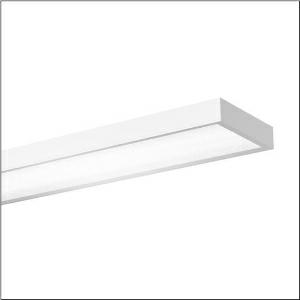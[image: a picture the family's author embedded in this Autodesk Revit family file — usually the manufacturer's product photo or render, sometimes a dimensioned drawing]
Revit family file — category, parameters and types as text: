
# Revit family: sport_31_51hs12dd4gca
name_source: partatom
category: Lighting Fixtures
units: mm (PartAtom-declared; Revit-internal decimal feet)

## family parameters
Cut with Voids When Loaded = No
Host = Face
Light Source = No
Part Type = Normal
Room Calculation Point = No
Round Connector Dimension = Use Diameter
Shared = No

## types (1)
- --- (1 x LED, 15290 lm, 113 W, 4000K)
    Apparent Load = 113 VA
    CIE Flux Codes = 65 89 97 100 100
    Color Rendering = 80
    Color Temperature = 4000K
    Default Elevation = 1800 mm
    Description = Sport 31, high bay luminaire, primary light control with reflector, of sheet steel, primary anti-glare with prismatic structure, of PC, primary optical cover: cover panel, of PC, light emission: direct distribution, primary light characteristic: symmetric, installation type: suspended mounting, recessed, surface-mounted, LED, rated luminous flux: 16.000lm, luminous efficacy: 137lm/W, light colour: 840, colour temperature: 4000K, control gear: DALI 2, with terminal, 5-pole, max. 2.5mm², mains connection: 220..240V, AC/DC, 50/60Hz, rated input power: 117W, housing, of sheet steel, traffic white (RAL 9016), length: 1.540mm, width: 415mm, height: 95mm, protection rating (complete): IP20, protection rating (lamp compartment, on room side): IP50, insulation class (complete): insulation class I (protective earthing), certification: CE, ENEC, UKCA, ball protection: ball impact resistant with ceiling mounting or chain suspension, impact resistance: IK08, permissible operating ambient temperature: -20..+35°C, standard: DIN 18032-3, EN 60598-2-22, packaging unit: 1 piece
    Height = 100 mm  [stored 0.328084 ft]
    Lamp = 1 x LED
    Lamp Light Flux = 15290 lm
    Lamp Power = 113 W
    Lamp count = 1
    Length = 1500 mm
    Luminous efficacy = 135 lm/W
    Manufacturer = Siteco
    ModVariant = No
    Model = 51HS12DD4GCA
    Mounting Place = Ceiling
    Mounting Type = Pendant
    Number of Poles = 1
    OnlyDefault = Yes
    Power Factor = 1
    Product Name = Sport 31
    Product group = high bay luminaire
    ProductGroupID = 901
    Protection Class = Protection class I
    Protection Degree = IP 20
    RLX_Detail_Level = 1
    RLX_Emergency_Light_Flux = 0 lm
    RLX_Emergency_Type = 0
    RLX_Emergency_Type_DB = No
    RlxData = <blob elided: 24053 chars, md5=e1513529>
    Socket = socket
    Standby Power = 0 W
    System Light Flux = 15290 lm
    System Power = 113 W
    Type Comments = factory setting: luminous flux: 100 % | dim-lin: 254 | 558 mA
    Type Image = l_1006829.jpg
    URL = http://relux.com
    VarID = @adj_218439
    Voltage = 0 V
    Weight = 0.00 kg
    Width = 415 mm

note: [stored X ft] marks values corroborated as IEEE doubles in the binary element streams (Revit-internal decimal feet)

## geometry (parser evidence)
native form markers: Blend x4, Sweep x11
no freeform markers — native parametric forms only
